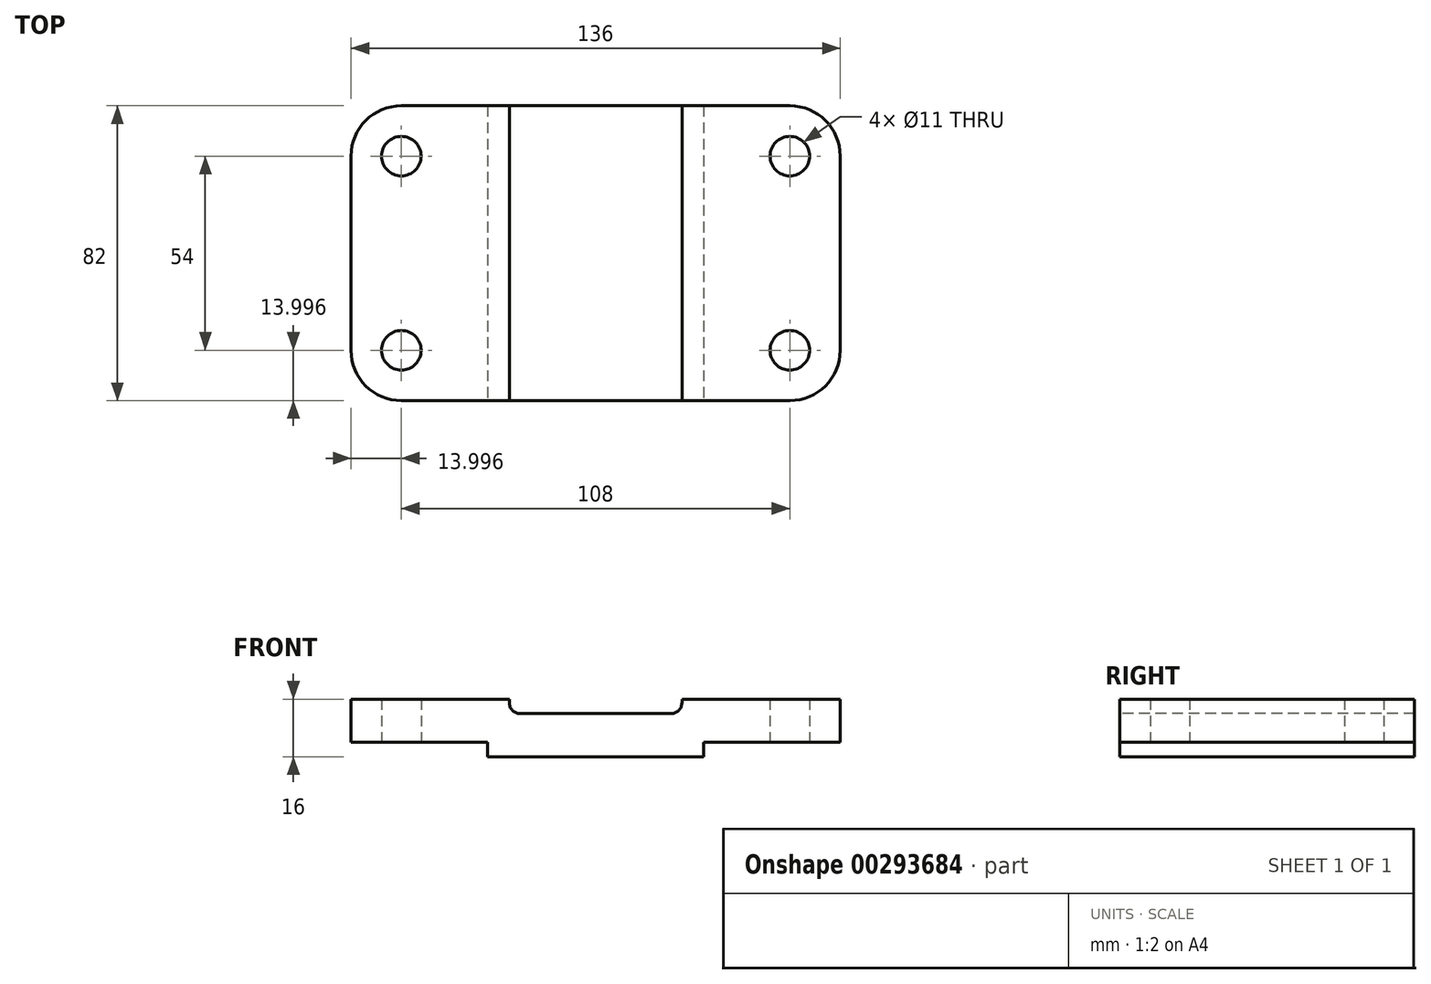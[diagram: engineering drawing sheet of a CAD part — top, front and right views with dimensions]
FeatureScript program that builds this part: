
annotation { "Feature Type Name" : "Feature", "Feature Type Description" : "" }
export const myFeature = defineFeature(function(context is Context, id is Id, definition is map)
    precondition{}
    {
        {
            var Q0;
            Q0=qCreatedBy(makeId("Top.planeOp"),FACE);
            var sketch = newSketch(context, id + "F0", { "sketchPlane" : qUnion([Q0])});
            skLineSegment(sketch, "E0.bottom", {"start": v(-27.61, 51.96) * mm, "end": v(80.39, 51.96) * mm});
            skLineSegment(sketch, "E0.top", {"start": v(-27.61, -30.04) * mm, "end": v(80.39, -30.04) * mm});
            skLineSegment(sketch, "E0.left", {"start": v(-41.61, 37.96) * mm, "end": v(-41.61, -16.04) * mm});
            skLineSegment(sketch, "E0.right", {"start": v(94.39, 37.96) * mm, "end": v(94.39, -16.04) * mm});
            skPoint(sketch, "E1.visualSharp", {"position": v(-41.61, 51.96) * mm});
            skArc(sketch, "E1.filletArc", {"start": v(-27.61, 51.96) * mm, "mid": v(-37.51, 47.86) * mm, "end": v(-41.61, 37.96) * mm});
            skPoint(sketch, "E2.visualSharp", {"position": v(94.39, 51.96) * mm});
            skArc(sketch, "E2.filletArc", {"start": v(94.39, 37.96) * mm, "mid": v(90.29, 47.86) * mm, "end": v(80.39, 51.96) * mm});
            skPoint(sketch, "E3.visualSharp", {"position": v(94.39, -30.04) * mm});
            skArc(sketch, "E3.filletArc", {"start": v(80.39, -30.04) * mm, "mid": v(90.29, -25.94) * mm, "end": v(94.39, -16.04) * mm});
            skPoint(sketch, "E4.visualSharp", {"position": v(-41.61, -30.04) * mm});
            skArc(sketch, "E4.filletArc", {"start": v(-41.61, -16.04) * mm, "mid": v(-37.51, -25.94) * mm, "end": v(-27.61, -30.04) * mm});
            skCircle(sketch, "E5", {"center": v(80.39, 37.96) * mm, "radius": 5.5 * mm});
            skCircle(sketch, "E6", {"center": v(80.39, -16.04) * mm, "radius": 5.5 * mm});
            skCircle(sketch, "E7", {"center": v(-27.61, -16.04) * mm, "radius": 5.5 * mm});
            skCircle(sketch, "E8", {"center": v(-27.61, 37.96) * mm, "radius": 5.5 * mm});
            skSolve(sketch);
        }
        {
            var Q0;
            Q0=makeQuery(id+"F0.imprint","IMPRINT",FACE,{"disambiguationData":[TD([[makeQuery(id+"F0.imprint","IMPRINT",EDGE,{"derivedFrom":sQuery(id+"F0.wireOp",EDGE,"E0.bottom")}),-1.0]])]});
            extrude(context, id + "F1", {"entities" : qUnion([Q0]), "depth" : 16 * mm});
        }
        {
            var Q0;
            Q0=makeQuery(id+"F1.opExtrude","SWEPT_FACE",FACE,{"disambiguationData":[OSD([sQuery(id+"F0.wireOp",EDGE,"E0.top")])]});
            var sketch = newSketch(context, id + "F2", { "sketchPlane" : qUnion([Q0])});
            skLineSegment(sketch, "E9.bottom", {"start": v(2.39, 16) * mm, "end": v(50.39, 16) * mm});
            skLineSegment(sketch, "E9.top", {"start": v(5.39, 12) * mm, "end": v(47.39, 12) * mm});
            skLineSegment(sketch, "E9.left", {"start": v(2.39, 16) * mm, "end": v(2.39, 15) * mm});
            skLineSegment(sketch, "E9.right", {"start": v(50.39, 16) * mm, "end": v(50.39, 15) * mm});
            skPoint(sketch, "E10.visualSharp", {"position": v(50.39, 12) * mm});
            skArc(sketch, "E10.filletArc", {"start": v(47.39, 12) * mm, "mid": v(49.5, 12.88) * mm, "end": v(50.39, 15) * mm});
            skPoint(sketch, "E11.visualSharp", {"position": v(2.39, 12) * mm});
            skArc(sketch, "E11.filletArc", {"start": v(2.39, 15) * mm, "mid": v(3.26, 12.88) * mm, "end": v(5.39, 12) * mm});
            skLineSegment(sketch, "E12.bottom", {"start": v(56.39, 4) * mm, "end": v(94.39, 4) * mm});
            skLineSegment(sketch, "E12.top", {"start": v(56.39, 0) * mm, "end": v(94.39, 0) * mm});
            skLineSegment(sketch, "E12.left", {"start": v(56.39, 4) * mm, "end": v(56.39, 0) * mm});
            skLineSegment(sketch, "E12.right", {"start": v(94.39, 4) * mm, "end": v(94.39, 0) * mm});
            skLineSegment(sketch, "E13.bottom", {"start": v(-41.61, 4) * mm, "end": v(-3.61, 4) * mm});
            skLineSegment(sketch, "E13.top", {"start": v(-41.61, 0) * mm, "end": v(-3.61, 0) * mm});
            skLineSegment(sketch, "E13.left", {"start": v(-41.61, 4) * mm, "end": v(-41.61, 0) * mm});
            skLineSegment(sketch, "E13.right", {"start": v(-3.61, 4) * mm, "end": v(-3.61, 0) * mm});
            skSolve(sketch);
        }
        {
            var Q0;
            Q0 = qSketchRegion(id + "F2", true);
            extrude(context, id + "F3", {"entities" : qUnion([Q0]), "operationType" : NewBodyOperationType.REMOVE, "endBound" : BoundingType.THROUGH_ALL, "oppositeDirection" : true, "depth" : 25 * mm});
        }
    });
